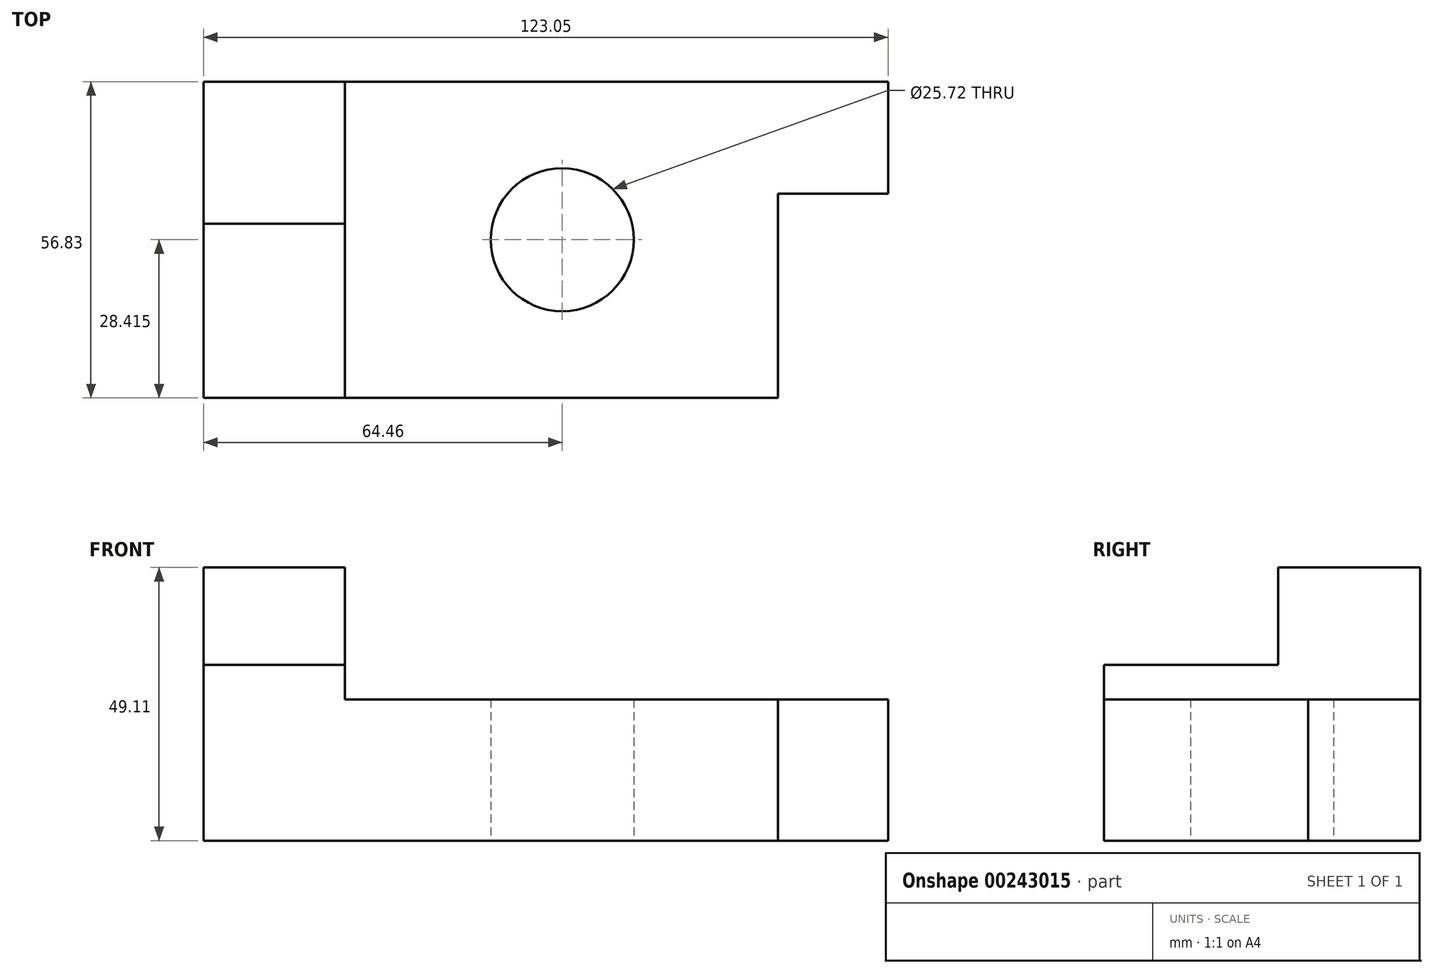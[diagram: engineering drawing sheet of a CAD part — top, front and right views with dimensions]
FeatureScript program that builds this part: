
annotation { "Feature Type Name" : "Feature", "Feature Type Description" : "" }
export const myFeature = defineFeature(function(context is Context, id is Id, definition is map)
    precondition{}
    {
        {
            var Q0;
            Q0=qCreatedBy(makeId("Top.planeOp"),FACE);
            var sketch = newSketch(context, id + "F0", { "sketchPlane" : qUnion([Q0])});
            skLineSegment(sketch, "E0.bottom", {"start": v(-39.06, 25.5) * mm, "end": v(38.77, 25.5) * mm});
            skLineSegment(sketch, "E0.top", {"start": v(-39.06, -31.33) * mm, "end": v(38.77, -31.33) * mm});
            skLineSegment(sketch, "E0.left", {"start": v(-39.06, 25.5) * mm, "end": v(-39.06, -31.33) * mm});
            skLineSegment(sketch, "E0.right", {"start": v(38.77, 25.5) * mm, "end": v(38.77, -31.33) * mm});
            skLineSegment(sketch, "E1.bottom", {"start": v(38.77, 25.5) * mm, "end": v(58.59, 25.5) * mm});
            skLineSegment(sketch, "E1.top", {"start": v(38.77, 5.4) * mm, "end": v(58.59, 5.4) * mm});
            skLineSegment(sketch, "E1.left", {"start": v(38.77, 25.5) * mm, "end": v(38.77, 5.4) * mm});
            skLineSegment(sketch, "E1.right", {"start": v(58.59, 25.5) * mm, "end": v(58.59, 5.4) * mm});
            skCircle(sketch, "E2", {"center": v(0, -2.91) * mm, "radius": 12.86 * mm});
            skPoint(sketch, "E2.centerSnap0", {"position": v(38.77, -2.91) * mm});
            skSolve(sketch);
        }
        {
            var Q0;
            Q0 = qSketchRegion(id + "F0", true);
            extrude(context, id + "F1", {"entities" : qUnion([Q0]), "depth" : 25.4 * mm});
        }
        {
            var Q0;
            Q0=makeQuery(id+"F1.opExtrude","SWEPT_FACE",FACE,{"disambiguationData":[OSD([sQuery(id+"F0.wireOp",EDGE,"E0.left")])]});
            var sketch = newSketch(context, id + "F2", { "sketchPlane" : qUnion([Q0])});
            skLineSegment(sketch, "E3.bottom", {"start": v(-25.5, 31.63) * mm, "end": v(31.33, 31.63) * mm});
            skLineSegment(sketch, "E3.top", {"start": v(-25.5, 0) * mm, "end": v(31.33, 0) * mm});
            skLineSegment(sketch, "E3.left", {"start": v(-25.5, 31.63) * mm, "end": v(-25.5, 0) * mm});
            skLineSegment(sketch, "E3.right", {"start": v(31.33, 31.63) * mm, "end": v(31.33, 0) * mm});
            skLineSegment(sketch, "E4.bottom", {"start": v(-25.5, 49.11) * mm, "end": v(0, 49.11) * mm});
            skLineSegment(sketch, "E4.top", {"start": v(-25.5, 31.63) * mm, "end": v(0, 31.63) * mm});
            skLineSegment(sketch, "E4.left", {"start": v(-25.5, 49.11) * mm, "end": v(-25.5, 31.63) * mm});
            skLineSegment(sketch, "E4.right", {"start": v(0, 49.11) * mm, "end": v(0, 31.63) * mm});
            skSolve(sketch);
        }
        {
            var Q0;
            Q0 = qSketchRegion(id + "F2", true);
            extrude(context, id + "F3", {"entities" : qUnion([Q0]), "operationType" : NewBodyOperationType.ADD, "depth" : 25.4 * mm});
        }
    });
